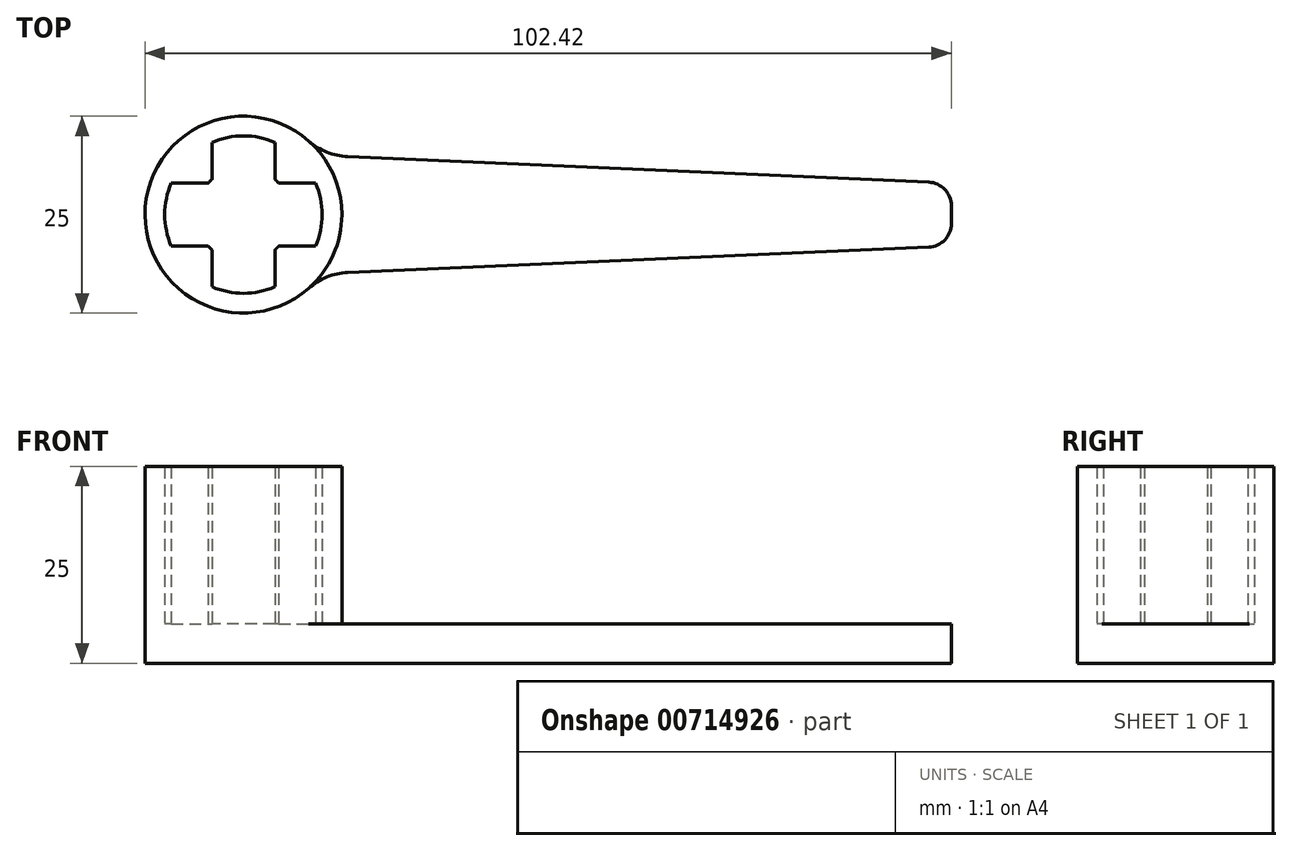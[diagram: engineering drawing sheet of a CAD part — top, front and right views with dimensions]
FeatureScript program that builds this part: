
annotation { "Feature Type Name" : "Feature", "Feature Type Description" : "" }
export const myFeature = defineFeature(function(context is Context, id is Id, definition is map)
    precondition{}
    {
        {
            var Q0;
            Q0=qCreatedBy(makeId("Top.planeOp"),FACE);
            var sketch = newSketch(context, id + "F0", { "sketchPlane" : qUnion([Q0])});
            skArc(sketch, "E0", {"start": v(-9.17, 4) * mm, "mid": v(-10, 0) * mm, "end": v(-9.17, -4) * mm});
            skArc(sketch, "E1", {"start": v(-4, 4.47) * mm, "mid": v(-4.24, 4.24) * mm, "end": v(-4.47, 4) * mm});
            skCircle(sketch, "E2", {"center": v(0, 0) * mm, "radius": 12.5 * mm});
            skLineSegment(sketch, "E3", {"start": v(-4, 9.17) * mm, "end": v(-4, 4.47) * mm});
            skLineSegment(sketch, "E4", {"start": v(4, 9.17) * mm, "end": v(4, 4.47) * mm});
            skLineSegment(sketch, "E5", {"start": v(-4, -4.47) * mm, "end": v(-4, -9.17) * mm});
            skLineSegment(sketch, "E6", {"start": v(4, -4.47) * mm, "end": v(4, -9.17) * mm});
            skLineSegment(sketch, "E7", {"start": v(-9.17, 4) * mm, "end": v(-4.47, 4) * mm});
            skLineSegment(sketch, "E8", {"start": v(4.47, 4) * mm, "end": v(9.17, 4) * mm});
            skLineSegment(sketch, "E9", {"start": v(-9.17, -4) * mm, "end": v(-4.47, -4) * mm});
            skLineSegment(sketch, "E10", {"start": v(4.47, -4) * mm, "end": v(9.17, -4) * mm});
            skLineSegment(sketch, "E11", {"start": v(-4, 9.17) * mm, "end": v(0, 9.17) * mm, "construction": true});
            skLineSegment(sketch, "E12", {"start": v(0, 9.17) * mm, "end": v(4, 9.17) * mm, "construction": true});
            skLineSegment(sketch, "E13", {"start": v(-9.17, -4) * mm, "end": v(-9.17, 4) * mm, "construction": true});
            skLineSegment(sketch, "E14", {"start": v(-4, -9.17) * mm, "end": v(4, -9.17) * mm, "construction": true});
            skArc(sketch, "E15.trimOffspring", {"start": v(4.47, 4) * mm, "mid": v(4.24, 4.24) * mm, "end": v(4, 4.47) * mm});
            skArc(sketch, "E16.trimOffspring", {"start": v(4, -4.47) * mm, "mid": v(4.24, -4.24) * mm, "end": v(4.47, -4) * mm});
            skArc(sketch, "E17.trimOffspring", {"start": v(-4.47, -4) * mm, "mid": v(-4.24, -4.24) * mm, "end": v(-4, -4.47) * mm});
            skArc(sketch, "E18.trimOffspring", {"start": v(4, 9.17) * mm, "mid": v(0, 10) * mm, "end": v(-4, 9.17) * mm});
            skArc(sketch, "E19.trimOffspring", {"start": v(9.17, -4) * mm, "mid": v(10, 0) * mm, "end": v(9.17, 4) * mm});
            skArc(sketch, "E20.trimOffspring", {"start": v(-4, -9.17) * mm, "mid": v(0, -10) * mm, "end": v(4, -9.17) * mm});
            skSolve(sketch);
        }
        {
            var Q0;
            Q0=makeQuery(id+"F0.imprint","IMPRINT",FACE,{"disambiguationData":[TD([[makeQuery(id+"F0.imprint","IMPRINT",EDGE,{"derivedFrom":sQuery(id+"F0.wireOp",EDGE,"E0")}),-1.0]])]});
            extrude(context, id + "F1", {"entities" : qUnion([Q0]), "depth" : 20 * mm, "offsetDistance" : 25 * mm});
        }
        {
            var Q0;
            Q0=qCreatedBy(makeId("Top.planeOp"),FACE);
            var sketch = newSketch(context, id + "F2", { "sketchPlane" : qUnion([Q0])});
            skCircle(sketch, "E21", {"center": v(0, 0) * mm, "radius": 12.5 * mm});
            skLineSegment(sketch, "E22", {"start": v(10, -7.5) * mm, "end": v(89.92, -4) * mm});
            skLineSegment(sketch, "E23", {"start": v(10, 7.5) * mm, "end": v(89.92, 4) * mm});
            skLineSegment(sketch, "E24", {"start": v(89.92, -4) * mm, "end": v(89.92, 0) * mm});
            skLineSegment(sketch, "E25", {"start": v(89.92, 0) * mm, "end": v(89.92, 4) * mm});
            skLineSegment(sketch, "E26", {"start": v(10, -7.5) * mm, "end": v(10, 7.5) * mm, "construction": true});
            skSolve(sketch);
        }
        {
            var Q0;
            Q0 = qSketchRegion(id + "F2", true);
            extrude(context, id + "F3", {"entities" : qUnion([Q0]), "operationType" : NewBodyOperationType.ADD, "oppositeDirection" : true, "depth" : 5 * mm, "offsetDistance" : 25 * mm});
        }
        {
            var Q0;
            Q0 = qSketchRegion(id + "F2", true);
            extrude(context, id + "F4", {"entities" : qUnion([Q0]), "operationType" : NewBodyOperationType.ADD, "oppositeDirection" : true, "depth" : 4 * mm, "offsetDistance" : 25 * mm});
        }
        {
            var Q0;
            Q0=makeQuery(id+"F3.opExtrude","SWEPT_EDGE",EDGE,{"disambiguationData":[OSD([sQuery(id+"F2.wireOp",EDGE,"E21"),sQuery(id+"F2.wireOp",EDGE,"E23")])]});
            var Q1;
            Q1=makeQuery(id+"F3.opExtrude","SWEPT_EDGE",EDGE,{"disambiguationData":[OSD([sQuery(id+"F2.wireOp",EDGE,"E21"),sQuery(id+"F2.wireOp",EDGE,"E22")])]});
            fillet(context, id + "F5", {"entities" : qUnion([Q0, Q1]), "radius" : 8 * mm, "tangentPropagation" : true, "allowEdgeOverflow" : false});
        }
        {
            var Q0;
            Q0=makeQuery(id+"F3.opExtrude","SWEPT_EDGE",EDGE,{"disambiguationData":[OSD([sQuery(id+"F2.wireOp",EDGE,"E23"),sQuery(id+"F2.wireOp",EDGE,"E25")])]});
            var Q1;
            Q1=makeQuery(id+"F3.opExtrude","SWEPT_EDGE",EDGE,{"disambiguationData":[OSD([sQuery(id+"F2.wireOp",EDGE,"E22"),sQuery(id+"F2.wireOp",EDGE,"E24")])]});
            fillet(context, id + "F6", {"entities" : qUnion([Q0, Q1]), "radius" : 3 * mm, "tangentPropagation" : true, "allowEdgeOverflow" : false});
        }
    });
